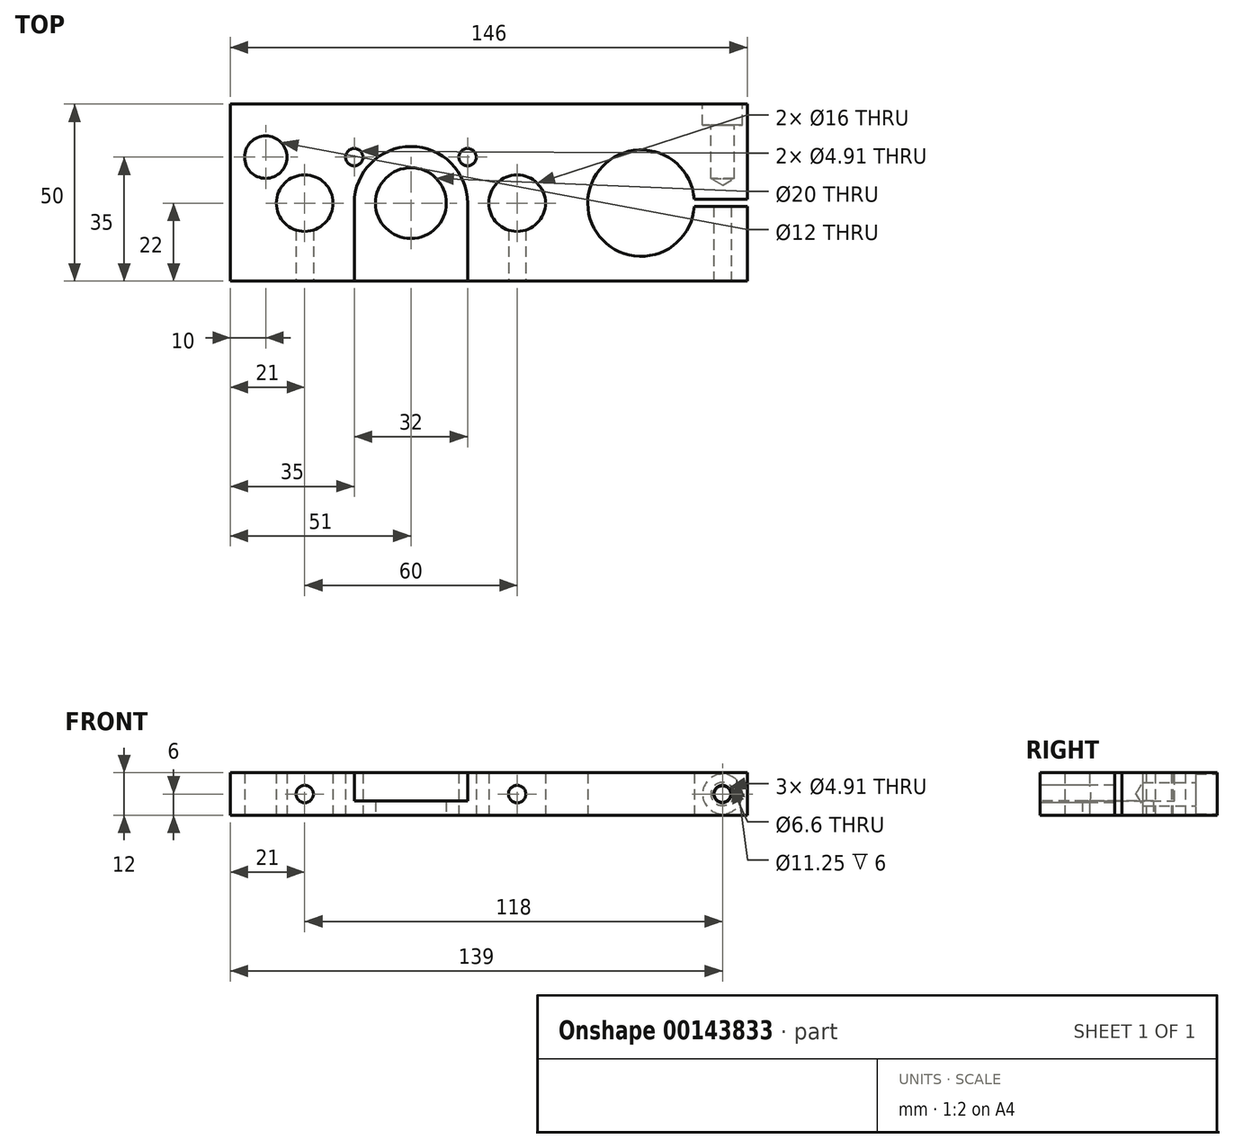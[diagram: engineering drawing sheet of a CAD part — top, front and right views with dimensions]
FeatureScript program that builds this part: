
annotation { "Feature Type Name" : "Feature", "Feature Type Description" : "" }
export const myFeature = defineFeature(function(context is Context, id is Id, definition is map)
    precondition{}
    {
        {
            var Q0;
            Q0=qCreatedBy(makeId("Top.planeOp"),FACE);
            var sketch = newSketch(context, id + "F0", { "sketchPlane" : qUnion([Q0])});
            skLineSegment(sketch, "E0.bottom", {"start": v(73, -25) * mm, "end": v(-73, -25) * mm});
            skLineSegment(sketch, "E0.top", {"start": v(73, 25) * mm, "end": v(-73, 25) * mm});
            skLineSegment(sketch, "E0.left", {"start": v(73, -25) * mm, "end": v(73, -3.93) * mm});
            skLineSegment(sketch, "E0.right", {"start": v(-73, -25) * mm, "end": v(-73, 25) * mm});
            skPoint(sketch, "E0.middle", {"position": v(0, 0) * mm});
            skCircle(sketch, "E1", {"center": v(8, -3) * mm, "radius": 8 * mm});
            skCircle(sketch, "E2", {"center": v(-52, -3) * mm, "radius": 8 * mm});
            skCircle(sketch, "E3", {"center": v(-22, -3) * mm, "radius": 10 * mm});
            skCircle(sketch, "E4", {"center": v(-38, 10) * mm, "radius": 2.46 * mm});
            skCircle(sketch, "E5", {"center": v(-6, 10) * mm, "radius": 2.46 * mm});
            skArc(sketch, "E6", {"start": v(58.01, -1.93) * mm, "mid": v(27.95, -3.07) * mm, "end": v(58.02, -3.93) * mm});
            skCircle(sketch, "E7", {"center": v(-63, 10) * mm, "radius": 6 * mm});
            skLineSegment(sketch, "E8.trimOffspring", {"start": v(73, -1.93) * mm, "end": v(73, 25) * mm});
            skLineSegment(sketch, "E9", {"start": v(73, -3.93) * mm, "end": v(58.02, -3.93) * mm});
            skLineSegment(sketch, "E10", {"start": v(73, -1.93) * mm, "end": v(58.01, -1.93) * mm});
            skSolve(sketch);
        }
        {
            var Q0;
            Q0=makeQuery(id+"F0.imprint","IMPRINT",FACE,{"disambiguationData":[TD([[makeQuery(id+"F0.imprint","IMPRINT",EDGE,{"derivedFrom":sQuery(id+"F0.wireOp",EDGE,"E0.bottom")}),-1.0]])]});
            extrude(context, id + "F1", {"entities" : qUnion([Q0]), "depth" : 12 * mm});
        }
        {
            var Q0;
            Q0=makeQuery(id+"F1.opExtrude","CAP_FACE",FACE,{"disambiguationData":[OSD([sQuery(id+"F0.wireOp",EDGE,"E0.bottom"),sQuery(id+"F0.wireOp",EDGE,"E0.top"),sQuery(id+"F0.wireOp",EDGE,"E0.left"),sQuery(id+"F0.wireOp",EDGE,"E0.right"),sQuery(id+"F0.wireOp",EDGE,"E1"),sQuery(id+"F0.wireOp",EDGE,"E2"),sQuery(id+"F0.wireOp",EDGE,"E3"),sQuery(id+"F0.wireOp",EDGE,"E4"),sQuery(id+"F0.wireOp",EDGE,"E5"),sQuery(id+"F0.wireOp",EDGE,"E6"),sQuery(id+"F0.wireOp",EDGE,"E7"),sQuery(id+"F0.wireOp",EDGE,"E8.trimOffspring"),sQuery(id+"F0.wireOp",EDGE,"E9"),sQuery(id+"F0.wireOp",EDGE,"E10")])],"isStart":false});
            var sketch = newSketch(context, id + "F2", { "sketchPlane" : qUnion([Q0])});
            skArc(sketch, "E11", {"start": v(-6, -3) * mm, "mid": v(-22, 13) * mm, "end": v(-38, -3) * mm});
            skLineSegment(sketch, "E12", {"start": v(-38, -3) * mm, "end": v(-38, -25) * mm});
            skLineSegment(sketch, "E13", {"start": v(-6, -3) * mm, "end": v(-6, -25) * mm});
            skSolve(sketch);
        }
        {
            var Q0;
            Q0=makeQuery(id+"F2.imprint","IMPRINT",FACE,{"disambiguationData":[TD([[makeQuery(id+"F2.imprint","IMPRINT",EDGE,{"derivedFrom":sQuery(id+"F2.wireOp",EDGE,"E11")}),1.0]])]});
            extrude(context, id + "F3", {"entities" : qUnion([Q0]), "operationType" : NewBodyOperationType.REMOVE, "oppositeDirection" : true, "depth" : 8 * mm});
        }
        {
            var Q0;
            Q0=makeQuery(id+"F1.opExtrude","SWEPT_FACE",FACE,{"disambiguationData":[OSD([sQuery(id+"F0.wireOp",EDGE,"E0.bottom")])]});
            var sketch = newSketch(context, id + "F4", { "sketchPlane" : qUnion([Q0])});
            skCircle(sketch, "E14", {"center": v(-52, 6) * mm, "radius": 2.46 * mm});
            skCircle(sketch, "E15", {"center": v(8, 6) * mm, "radius": 2.46 * mm});
            skCircle(sketch, "E16", {"center": v(66, 6) * mm, "radius": 2.46 * mm});
            skSolve(sketch);
        }
        {
            var Q0;
            Q0=sQuery(id+"F4.wireOp",VERTEX,"E14.center");
            var Q1;
            Q1=sQuery(id+"F4.wireOp",VERTEX,"E15.center");
            var Q2;
            Q2=makeQuery(id+"F1.opExtrude","SWEPT_BODY",BODY,{"disambiguationData":[OSD([sQuery(id+"F0.wireOp",EDGE,"E0.bottom"),sQuery(id+"F0.wireOp",EDGE,"E0.top"),sQuery(id+"F0.wireOp",EDGE,"E0.left"),sQuery(id+"F0.wireOp",EDGE,"E0.right"),sQuery(id+"F0.wireOp",EDGE,"E1"),sQuery(id+"F0.wireOp",EDGE,"E2"),sQuery(id+"F0.wireOp",EDGE,"E3"),sQuery(id+"F0.wireOp",EDGE,"E4"),sQuery(id+"F0.wireOp",EDGE,"E5"),sQuery(id+"F0.wireOp",EDGE,"E6"),sQuery(id+"F0.wireOp",EDGE,"E7"),sQuery(id+"F0.wireOp",EDGE,"E8.trimOffspring"),sQuery(id+"F0.wireOp",EDGE,"E9"),sQuery(id+"F0.wireOp",EDGE,"E10")])]});
            hole(context, id + "F5", {"style" : HoleStyle.SIMPLE, "endStyle" : HoleEndStyle.BLIND, "holeDiameter" : 4.9 * mm, "holeDepth" : 20 * mm, "startFromSketch" : true, "locations" : qUnion([Q0, Q1]), "scope" : qUnion([Q2])});
        }
        {
            var Q0;
            Q0=sQuery(id+"F4.wireOp",VERTEX,"E16.center");
            var Q1;
            Q1=makeQuery(id+"F1.opExtrude","SWEPT_BODY",BODY,{"disambiguationData":[OSD([sQuery(id+"F0.wireOp",EDGE,"E0.bottom"),sQuery(id+"F0.wireOp",EDGE,"E0.top"),sQuery(id+"F0.wireOp",EDGE,"E0.left"),sQuery(id+"F0.wireOp",EDGE,"E0.right"),sQuery(id+"F0.wireOp",EDGE,"E1"),sQuery(id+"F0.wireOp",EDGE,"E2"),sQuery(id+"F0.wireOp",EDGE,"E3"),sQuery(id+"F0.wireOp",EDGE,"E4"),sQuery(id+"F0.wireOp",EDGE,"E5"),sQuery(id+"F0.wireOp",EDGE,"E6"),sQuery(id+"F0.wireOp",EDGE,"E7"),sQuery(id+"F0.wireOp",EDGE,"E8.trimOffspring"),sQuery(id+"F0.wireOp",EDGE,"E9"),sQuery(id+"F0.wireOp",EDGE,"E10")])]});
            hole(context, id + "F6", {"style" : HoleStyle.SIMPLE, "endStyle" : HoleEndStyle.BLIND, "holeDiameter" : 4.9 * mm, "holeDepth" : 21 * mm, "startFromSketch" : true, "locations" : qUnion([Q0]), "scope" : qUnion([Q1])});
        }
        {
            var Q0;
            Q0=makeQuery(id+"F1.opExtrude","SWEPT_FACE",FACE,{"disambiguationData":[OSD([sQuery(id+"F0.wireOp",EDGE,"E0.top")])]});
            var sketch = newSketch(context, id + "F7", { "sketchPlane" : qUnion([Q0])});
            skCircle(sketch, "E17", {"center": v(-66, 6) * mm, "radius": 2.46 * mm});
            skSolve(sketch);
        }
        {
            var Q0;
            Q0=sQuery(id+"F7.wireOp",VERTEX,"E17.center");
            var Q1;
            Q1=makeQuery(id+"F1.opExtrude","SWEPT_BODY",BODY,{"disambiguationData":[OSD([sQuery(id+"F0.wireOp",EDGE,"E0.bottom"),sQuery(id+"F0.wireOp",EDGE,"E0.top"),sQuery(id+"F0.wireOp",EDGE,"E0.left"),sQuery(id+"F0.wireOp",EDGE,"E0.right"),sQuery(id+"F0.wireOp",EDGE,"E1"),sQuery(id+"F0.wireOp",EDGE,"E2"),sQuery(id+"F0.wireOp",EDGE,"E3"),sQuery(id+"F0.wireOp",EDGE,"E4"),sQuery(id+"F0.wireOp",EDGE,"E5"),sQuery(id+"F0.wireOp",EDGE,"E6"),sQuery(id+"F0.wireOp",EDGE,"E7"),sQuery(id+"F0.wireOp",EDGE,"E8.trimOffspring"),sQuery(id+"F0.wireOp",EDGE,"E9"),sQuery(id+"F0.wireOp",EDGE,"E10")])]});
            hole(context, id + "F8", {"style" : HoleStyle.C_BORE, "endStyle" : HoleEndStyle.BLIND, "standardTappedOrClearance" : lookupTablePath({ "standard" : "ISO", "fit" : "Normal", "size" : "M6", "type" : "Clearance" }), "standardBlindInLast" : lookupTablePath({ "fit" : "Standard", "standard" : "ISO", "size" : "M6", "type" : "Clearance" }), "holeDiameter" : 6.6 * mm, "cBoreDiameter" : 11.25 * mm, "cBoreDepth" : 6 * mm, "holeDepth" : 21 * mm, "startFromSketch" : true, "locations" : qUnion([Q0]), "scope" : qUnion([Q1])});
        }
    });
